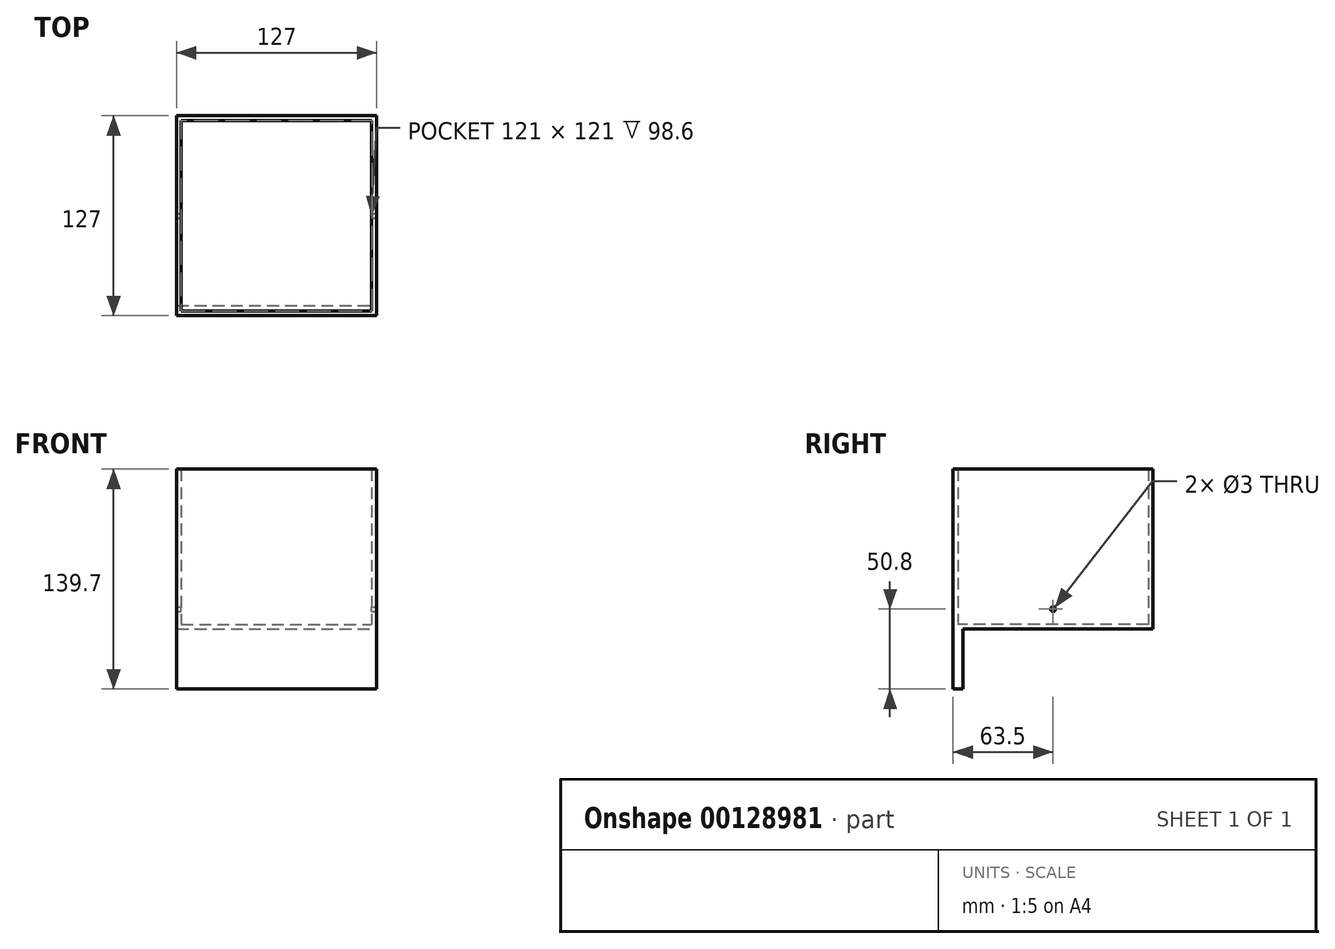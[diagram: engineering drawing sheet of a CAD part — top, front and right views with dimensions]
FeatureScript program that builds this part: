
annotation { "Feature Type Name" : "Feature", "Feature Type Description" : "" }
export const myFeature = defineFeature(function(context is Context, id is Id, definition is map)
    precondition{}
    {
        {
            var Q0;
            Q0=qCreatedBy(makeId("Top.planeOp"),FACE);
            var sketch = newSketch(context, id + "F0", { "sketchPlane" : qUnion([Q0])});
            skLineSegment(sketch, "E0.bottom", {"start": v(-63.5, 63.5) * mm, "end": v(63.5, 63.5) * mm});
            skLineSegment(sketch, "E0.top", {"start": v(-63.5, -63.5) * mm, "end": v(63.5, -63.5) * mm});
            skLineSegment(sketch, "E0.left", {"start": v(-63.5, 63.5) * mm, "end": v(-63.5, -63.5) * mm});
            skLineSegment(sketch, "E0.right", {"start": v(63.5, 63.5) * mm, "end": v(63.5, -63.5) * mm});
            skPoint(sketch, "E0.middle", {"position": v(0, 0) * mm});
            skCircle(sketch, "E1", {"center": v(0, 0) * mm, "radius": 95.25 * mm, "construction": true});
            skSolve(sketch);
        }
        {
            var Q0;
            Q0=makeQuery(id+"F0.imprint","IMPRINT",FACE,{"disambiguationData":[TD([[makeQuery(id+"F0.imprint","IMPRINT",EDGE,{"derivedFrom":sQuery(id+"F0.wireOp",EDGE,"E0.bottom")}),-1.0]])]});
            extrude(context, id + "F1", {"entities" : qUnion([Q0]), "depth" : 101.6 * mm});
        }
        {
            var Q0;
            Q0=makeQuery(id+"F1.opExtrude","CAP_FACE",FACE,{"disambiguationData":[OSD([sQuery(id+"F0.wireOp",EDGE,"E0.bottom"),sQuery(id+"F0.wireOp",EDGE,"E0.top"),sQuery(id+"F0.wireOp",EDGE,"E0.left"),sQuery(id+"F0.wireOp",EDGE,"E0.right")])],"isStart":false});
            shell(context, id + "F2", {"entities" : qUnion([Q0]), "thickness" : 3 * mm});
        }
        {
            var Q0;
            Q0=makeQuery(id+"F1.opExtrude","SWEPT_FACE",FACE,{"disambiguationData":[OSD([sQuery(id+"F0.wireOp",EDGE,"E0.right")])]});
            var sketch = newSketch(context, id + "F3", { "sketchPlane" : qUnion([Q0])});
            skLineSegment(sketch, "E2", {"start": v(0, 0) * mm, "end": v(0, 101.6) * mm, "construction": true});
            skPoint(sketch, "E3", {"position": v(0, 50.8) * mm});
            skLineSegment(sketch, "E4", {"start": v(0, 50.8) * mm, "end": v(63.5, 50.8) * mm, "construction": true});
            skLineSegment(sketch, "E5", {"start": v(0, 50.8) * mm, "end": v(31.75, 50.8) * mm, "construction": true});
            skLineSegment(sketch, "E6", {"start": v(15.88, 50.8) * mm, "end": v(15.88, 0) * mm, "construction": true});
            skLineSegment(sketch, "E7", {"start": v(15.88, 0) * mm, "end": v(15.88, 25.4) * mm, "construction": true});
            skPoint(sketch, "E8", {"position": v(15.88, 12.7) * mm});
            skCircle(sketch, "E9", {"center": v(15.88, 12.7) * mm, "radius": 63.5 * mm, "construction": true});
            skLineSegment(sketch, "E10", {"start": v(15.88, 12.7) * mm, "end": v(0, 12.7) * mm, "construction": true});
            skPoint(sketch, "E11", {"position": v(0, 12.7) * mm});
            skSolve(sketch);
        }
        {
            var Q0;
            Q0=makeQuery(id+"F1.opExtrude","SWEPT_FACE",FACE,{"disambiguationData":[OSD([sQuery(id+"F0.wireOp",EDGE,"E0.top")])]});
            var sketch = newSketch(context, id + "F4", { "sketchPlane" : qUnion([Q0])});
            skLineSegment(sketch, "E12", {"start": v(63.5, 0) * mm, "end": v(63.5, -38.1) * mm});
            skLineSegment(sketch, "E13", {"start": v(-63.5, 0) * mm, "end": v(-63.5, -38.1) * mm});
            skLineSegment(sketch, "E14", {"start": v(-63.5, -38.1) * mm, "end": v(63.5, -38.1) * mm});
            skSolve(sketch);
        }
        {
            var Q0;
            Q0=makeQuery(id+"F4.imprint","IMPRINT",FACE,{"disambiguationData":[TD([[makeQuery(id+"F4.imprint","IMPRINT",EDGE,{"derivedFrom":sQuery(id+"F4.wireOp",EDGE,"E12")}),-1.0]])]});
            extrude(context, id + "F5", {"entities" : qUnion([Q0]), "operationType" : NewBodyOperationType.ADD, "oppositeDirection" : true, "depth" : 6.35 * mm});
        }
        {
            var Q0;
            Q0=sQuery(id+"F3.wireOp",VERTEX,"E11");
            var Q1;
            Q1=makeQuery(id+"F1.opExtrude","SWEPT_BODY",BODY,{"disambiguationData":[OSD([sQuery(id+"F0.wireOp",EDGE,"E0.bottom"),sQuery(id+"F0.wireOp",EDGE,"E0.top"),sQuery(id+"F0.wireOp",EDGE,"E0.left"),sQuery(id+"F0.wireOp",EDGE,"E0.right")])]});
            hole(context, id + "F6", {"style" : HoleStyle.SIMPLE, "endStyle" : HoleEndStyle.THROUGH, "holeDiameter" : 3 * mm, "locations" : qUnion([Q0]), "scope" : qUnion([Q1]), "isTappedThrough" : true});
        }
    });
